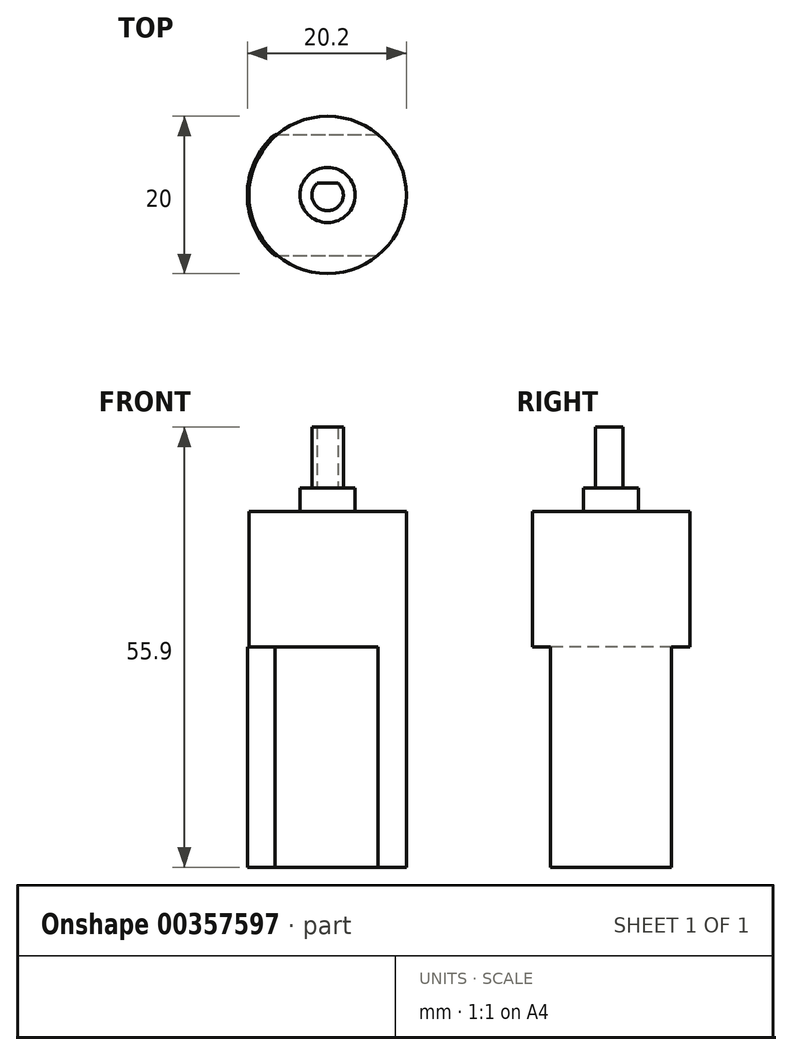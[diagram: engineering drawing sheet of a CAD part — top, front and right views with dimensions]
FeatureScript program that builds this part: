
annotation { "Feature Type Name" : "Feature", "Feature Type Description" : "" }
export const myFeature = defineFeature(function(context is Context, id is Id, definition is map)
    precondition{}
    {
        {
            var Q0;
            Q0=qCreatedBy(makeId("Top.planeOp"),FACE);
            var sketch = newSketch(context, id + "F0", { "sketchPlane" : qUnion([Q0])});
            skCircle(sketch, "E0", {"center": v(0, 0) * mm, "radius": 10 * mm});
            skCircle(sketch, "E1", {"center": v(0, 0) * mm, "radius": 3.5 * mm});
            skArc(sketch, "E2", {"start": v(-1.32, 1.5) * mm, "mid": v(0, -2) * mm, "end": v(1.32, 1.5) * mm});
            skLineSegment(sketch, "E3", {"start": v(-1.32, 1.5) * mm, "end": v(1.32, 1.5) * mm});
            skSolve(sketch);
        }
        {
            var Q0;
            Q0=makeQuery(id+"F0.imprint","IMPRINT",FACE,{"disambiguationData":[TD([[makeQuery(id+"F0.imprint","IMPRINT",EDGE,{"derivedFrom":sQuery(id+"F0.wireOp",EDGE,"E1")}),1.0]])]});
            var Q1;
            {var subQ0=sQuery(id+"F0.wireOp",EDGE,"E3");Q1=makeQuery(id+"F0.imprint","IMPRINT",FACE,{"disambiguationData":[TD([[makeQuery(id+"F0.imprint","IMPRINT",EDGE,{"derivedFrom":subQ0}),-1.0]])]});}
            var Q2;
            Q2=makeQuery(id+"F0.imprint","IMPRINT",FACE,{"disambiguationData":[TD([[makeQuery(id+"F0.imprint","IMPRINT",EDGE,{"derivedFrom":sQuery(id+"F0.wireOp",EDGE,"E0")}),1.0]])]});
            var Q3;
            {var subQ0=sQuery(id+"F0.wireOp",EDGE,"E3");Q3=makeQuery(id+"F0.imprint","IMPRINT",FACE,{"disambiguationData":[TD([[makeQuery(id+"F0.imprint","IMPRINT",EDGE,{"derivedFrom":subQ0}),1.0]])]});}
            extrude(context, id + "F1", {"entities" : qUnion([Q0, Q1, Q2, Q3]), "oppositeDirection" : true, "depth" : 17.2 * mm});
        }
        {
            var Q0;
            Q0=makeQuery(id+"F0.imprint","IMPRINT",FACE,{"disambiguationData":[TD([[makeQuery(id+"F0.imprint","IMPRINT",EDGE,{"derivedFrom":sQuery(id+"F0.wireOp",EDGE,"E1")}),1.0]])]});
            var Q1;
            {var subQ0=sQuery(id+"F0.wireOp",EDGE,"E3");Q1=makeQuery(id+"F0.imprint","IMPRINT",FACE,{"disambiguationData":[TD([[makeQuery(id+"F0.imprint","IMPRINT",EDGE,{"derivedFrom":subQ0}),1.0]])]});}
            var Q2;
            {var subQ0=sQuery(id+"F0.wireOp",EDGE,"E3");Q2=makeQuery(id+"F0.imprint","IMPRINT",FACE,{"disambiguationData":[TD([[makeQuery(id+"F0.imprint","IMPRINT",EDGE,{"derivedFrom":subQ0}),-1.0]])]});}
            extrude(context, id + "F2", {"entities" : qUnion([Q0, Q1, Q2]), "operationType" : NewBodyOperationType.ADD, "depth" : 3 * mm});
        }
        {
            var Q0;
            {var subQ0=sQuery(id+"F0.wireOp",EDGE,"E3");Q0=makeQuery(id+"F0.imprint","IMPRINT",FACE,{"disambiguationData":[TD([[makeQuery(id+"F0.imprint","IMPRINT",EDGE,{"derivedFrom":subQ0}),-1.0]])]});}
            extrude(context, id + "F3", {"entities" : qUnion([Q0]), "operationType" : NewBodyOperationType.ADD, "depth" : 10.7 * mm});
        }
        {
            var Q0;
            Q0=makeQuery(id+"F1.opExtrude","CAP_FACE",FACE,{"disambiguationData":[OSD([sQuery(id+"F0.wireOp",EDGE,"E0")])],"isStart":false});
            var sketch = newSketch(context, id + "F4", { "sketchPlane" : qUnion([Q0])});
            skArc(sketch, "E4", {"start": v(6.69, 7.7) * mm, "mid": v(10.2, 0) * mm, "end": v(6.69, -7.7) * mm});
            skArc(sketch, "E5.MirrorCS", {"start": v(-6.69, 7.7) * mm, "mid": v(-10.2, 0) * mm, "end": v(-6.69, -7.7) * mm});
            skLineSegment(sketch, "E6", {"start": v(-6.69, 7.7) * mm, "end": v(6.69, 7.7) * mm});
            skLineSegment(sketch, "E7.MirrorCS", {"start": v(-6.69, -7.7) * mm, "end": v(6.69, -7.7) * mm});
            skSolve(sketch);
        }
        {
            var Q0;
            {var subQ0=sQuery(id+"F4.wireOp",EDGE,"E5.MirrorCS");Q0=makeQuery(id+"F4.imprint","IMPRINT",FACE,{"disambiguationData":[TD([[makeQuery(id+"F4.imprint","IMPRINT",EDGE,{"derivedFrom":subQ0}),1.0]])]});}
            var Q1;
            {var subQ0=sQuery(id+"F4.wireOp",EDGE,"E6");var subQ1=makeQuery(id+"F1.opExtrude","CAP_EDGE",EDGE,{"disambiguationData":[OSD([sQuery(id+"F0.wireOp",EDGE,"E0")])],"isStart":false});var subQ2=makeQuery(id+"F4.imprint","INTERSECT",VERTEX,{"disambiguationData":[OD(0.0)],"derivedFrom":[subQ1,subQ0]});Q1=makeQuery(id+"F4.imprint","IMPRINT",FACE,{"disambiguationData":[TD([[makeQuery(id+"F4.imprint","IMPRINT",EDGE,{"disambiguationData":[TD([[subQ2,-1.0]])],"derivedFrom":subQ0}),-1.0]])]});}
            var Q2;
            {var subQ0=sQuery(id+"F4.wireOp",EDGE,"E4");Q2=makeQuery(id+"F4.imprint","IMPRINT",FACE,{"disambiguationData":[TD([[makeQuery(id+"F4.imprint","IMPRINT",EDGE,{"derivedFrom":subQ0}),-1.0]])]});}
            extrude(context, id + "F5", {"entities" : qUnion([Q0, Q1, Q2]), "operationType" : NewBodyOperationType.ADD, "depth" : 28 * mm});
        }
    });
